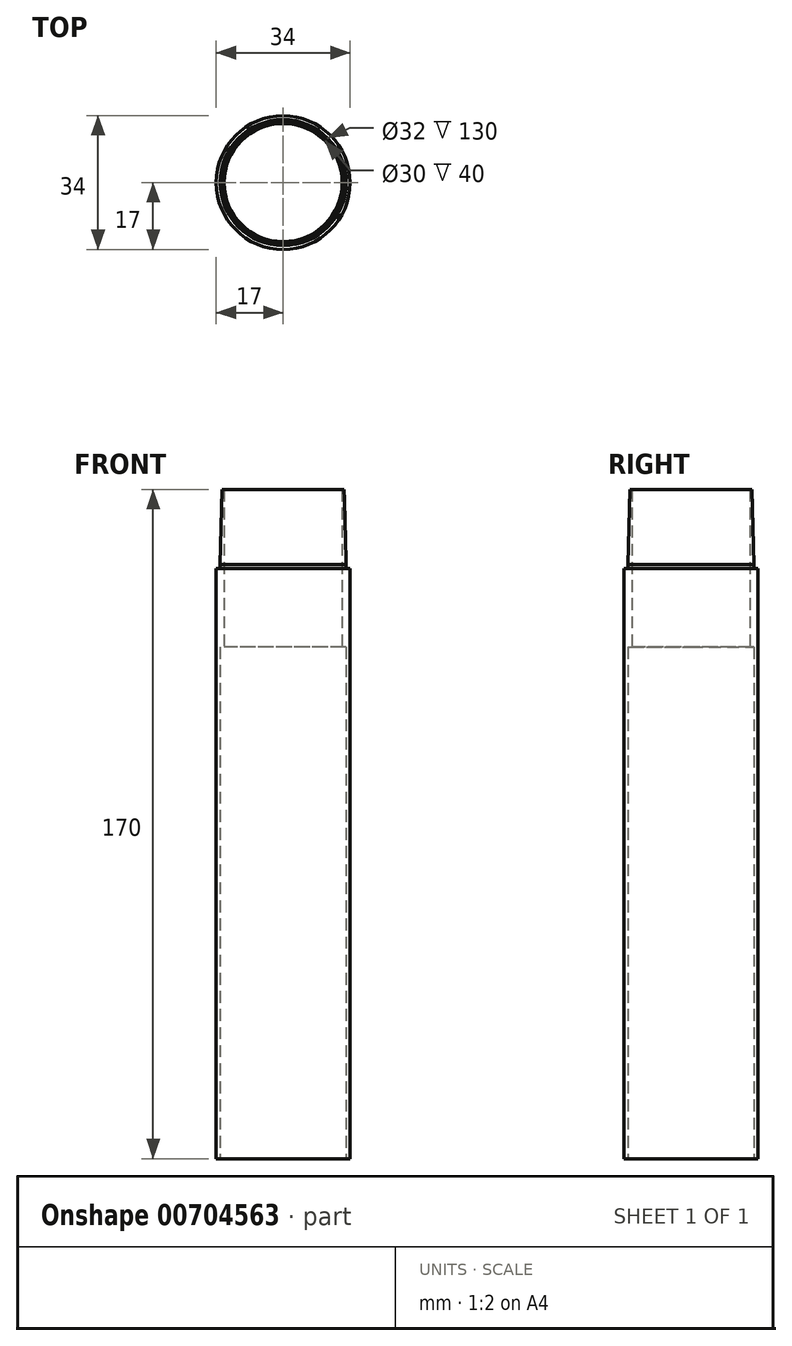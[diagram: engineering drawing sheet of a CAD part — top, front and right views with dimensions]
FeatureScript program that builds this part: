
annotation { "Feature Type Name" : "Feature", "Feature Type Description" : "" }
export const myFeature = defineFeature(function(context is Context, id is Id, definition is map)
    precondition{}
    {
        {
            var Q0;
            Q0=qCreatedBy(makeId("Top.planeOp"),FACE);
            var sketch = newSketch(context, id + "F0", { "sketchPlane" : qUnion([Q0])});
            skCircle(sketch, "E0", {"center": v(0, 0) * mm, "radius": 17 * mm});
            skCircle(sketch, "E1", {"center": v(0, 0) * mm, "radius": 16 * mm});
            skSolve(sketch);
        }
        {
            var Q0;
            Q0 = qSketchRegion(id + "F0", true);
            extrude(context, id + "F1", {"entities" : qUnion([Q0]), "depth" : 150 * mm, "offsetDistance" : 25 * mm});
        }
        {
            var Q0;
            Q0=makeQuery(id+"F1.opExtrude","CAP_FACE",FACE,{"disambiguationData":[OSD([sQuery(id+"F0.wireOp",EDGE,"E0"),sQuery(id+"F0.wireOp",EDGE,"E1")])],"isStart":false});
            var sketch = newSketch(context, id + "F2", { "sketchPlane" : qUnion([Q0])});
            skCircle(sketch, "E2", {"center": v(0, 0) * mm, "radius": 16 * mm});
            skCircle(sketch, "E3", {"center": v(0, 0) * mm, "radius": 15 * mm});
            skSolve(sketch);
        }
        {
            var Q0;
            Q0 = qSketchRegion(id + "F2", true);
            extrude(context, id + "F3", {"entities" : qUnion([Q0]), "operationType" : NewBodyOperationType.ADD, "depth" : 20 * mm, "offsetDistance" : 25 * mm, "hasSecondDirection" : true, "secondDirectionOppositeDirection" : true, "secondDirectionDepth" : 20 * mm});
        }
        {
            var Q0;
            Q0=makeQuery(id+"F3.opExtrude","CAP_EDGE",EDGE,{"disambiguationData":[OSD([sQuery(id+"F2.wireOp",EDGE,"E2")])],"isStart":false});
            chamfer(context, id + "F4", {"entities" : qUnion([Q0]), "chamferType" : ChamferType.OFFSET_ANGLE, "width" : 0.5 * mm, "oppositeDirection" : false, "angle" : 88.5 * degree, "tangentPropagation" : true});
        }
    });
